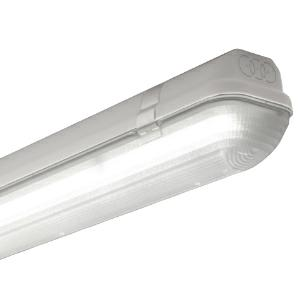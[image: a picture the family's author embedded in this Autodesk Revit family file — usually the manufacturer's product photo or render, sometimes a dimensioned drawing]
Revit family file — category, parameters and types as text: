
# Revit family: 3f_filippi_-_3f_linda_3f_filippi_-_58590_-_3f_linda_led_1x24w-865_ep_l1270
name_source: partatom
category: Lighting Fixtures
units: mm (PartAtom-declared; Revit-internal decimal feet)

## family parameters
Cut with Voids When Loaded = No
Host = Face
Light Source = No
Part Type = Normal
Room Calculation Point = No
Round Connector Dimension = Use Diameter
Shared = No

## types (1)
- 3F Filippi - 3F Linda (1 x LED, 4065 lm, 29 W, 6500 K)
    Apparent Load = 29 VA
    Approval mark = ENEC
    CIE Flux Codes = 44 77 94 97 100
    Color Rendering = 80
    Color Temperature = 6500 K
    Control Gear = Electronic ballast
    Default Elevation = 1800 mm
    Description = ILLUMINOTECHNICAL
Luminous efficiency 100% (DLOR 97%, ULOR 3%).
Initial luminous flux of the luminaire 4065 lm.
Emergency luminaire luminous flux BLF 14.3%.
Controlled symmetric distribution.
Installation Interdistance Transv.D = 1.77 x hu - Long.D = 1.17 x hu.
Tabular UGR (CIE 117 - 4H-8H; S=0.25H; 70/50/20): RUG 22 - 22.9.
Beam angle: 109° - 64°.
Luminous efficacy 140 lm/W.
Lifetime (L93/B10): 30000 h. (tq+25°C)
Lifetime (L90/B10): 50000 h. (tq+25°C)
Lifetime (L85/B10): 80000 h. (tq+25°C)
Lifetime (L80/B10): 100000 h. (tq+25°C)
Sudden decreased luminous flux after 50000 hours: 0% (C0).
Photobiological safety in compliance with IEC/TR 62778: RG0 risk exempt, (IEC 62471).
In compliance with IEC/EN 62722-2-1 - IEC/EN 62717 standards.

SOURCE
Linear LED module 24W/865.
Energy efficiency class (UE 2019/2020 - UE 2019/2015): D.
CIE 13.3 Colour rendering index: CRI >80 (R9 <50%).
IES TM-30 Fidelity Index: Rf = 84 Rg = 95.
CCT nominal colour temperature 6500 K.
Colour initial tolerance (MacAdam): SDCM 3.

MECHANICAL
Self-extinguishing V2 polycarbonate housing, injection moulded, RAL 7035 grey.
Ecologic anti-aging injected sealing gasket.
Diffuser in self-extinguishing V2 polycarbonate, photo-engraved interior, UV stabilised, injection moulded with smooth outer surface, tamper-proof opening.
Gear-holder reflector in hot-dip galvanised steel, painted with white polyester base.
Snug fit safety snap-lock clips for diffuser mounting in stainless steel, screwdriver opening.
Fixing brackets in stainless steel.
Possibility for technicians to access the interior of the luminaire.
Luminaire with limited surface temperature. - D - (EN 60598-2-24)
Dimensions: 1270x100 mm, height 100 mm. Weight 2.485 kg.
IP66 protection degree.
Mechanical strength to impacts IK10 (20 joule).
Glow-wire test resistance 850°C.

ELECTRICAL
Halogen Free electronic wiring 230V-50/60Hz, power factor 0.90, THD <25%, constant output current, SELV, class I, 1 driver.
Power of the luminaire 29 W.
CE - IEC 60598-1 - EN 60598-1.
EP maintained emergency wiring on board, 1h duration, 24h recharge; compliant with EN 60598-2-22, excluding high risk areas.
SAFE FLICKER: PstLM=<1 and SVM=<0.4 (IEC TR 61547-1 and IEC TR 63158), to ensure a more comfortable and safe light.
Ambient temperature from +5°C to +25°C.
Temperature class T6 max 85°C.
Relative humidity UR: <85%.

INSTALLATION
Ceiling / Suspended / Wall.
All accessories dedicated to this product are available on the Catalog and on our website www.3F-Filippi.com.

APPLICATIONS
Suitable product for food production plants (HACCP), IFS (Food Version 6), BRC (GSFS Food Version 7).
Dry, dusty indoor environments, subject to occasional water splashes.
Virtually shatterproof polycarbonate compatibly with the fumes / atmospheres that compromise the elasticity of plastic materials.
Not suitable for installation on surfaces subject to important vibrations, exposed to weather conditions, on ropes or poles.
Suitable for illumination of public car parks and parking grounds referred to DIN 67528:2018-04.

WARNING
Fixture not suitable for cold stores with an ambient temperature <5°C and/or relative humidity >85%.
Luminaire designed for disposal/recycling at end-of-life.
Replaceable (LED only) light source by a professional. Replaceable control gear by a professional.
    Height = 100 mm  [stored 0.328084 ft]
    Lamp = 1 x LED
    Lamp Light Flux = 4065 lm
    Lamp Power = 29 W
    Lamp count = 1
    Length = 1270 mm
    Lifetime = 50000 h
    Luminous efficacy = 140 lm/W
    Manufacturer = 3F Filippi
    ModVariant = No
    Model = 3F Filippi - 58590 - 3F Linda LED 1x24W-865 EP L1270
    Mounting Place = Ceiling
    Mounting Type = Pendant
    Number of Poles = 1
    OnlyDefault = Yes
    Power Factor = 1
    Product Name = 3F Filippi - 3F Linda
    Product group = pendant luminaire
    ProductGroupID = 9
    Protection Class = Protection class I
    Protection Degree = IP 66
    RLX_Detail_Level = 1
    RLX_Emergency_Light_Flux = 0 lm
    RLX_Emergency_Type = 0
    RLX_Emergency_Type_DB = No
    RlxData = <blob elided: 70489 chars, md5=1738b0d8>
    Socket = socket
    Standby Power = 0 W
    System Light Flux = 4065 lm
    System Power = 29 W
    Type Comments = Product without accessories
    Type Image = 3ffilippi_3f_linda_led.jpg
    URL = http://relux.com
    VarID = ---
    Voltage = 0 V
    Weight = 0.00 kg
    Width = 100 mm  [stored 0.328084 ft]

note: [stored X ft] marks values corroborated as IEEE doubles in the binary element streams (Revit-internal decimal feet)

## geometry (parser evidence)
native form markers: Blend x4, Sweep x8
no freeform markers — native parametric forms only
